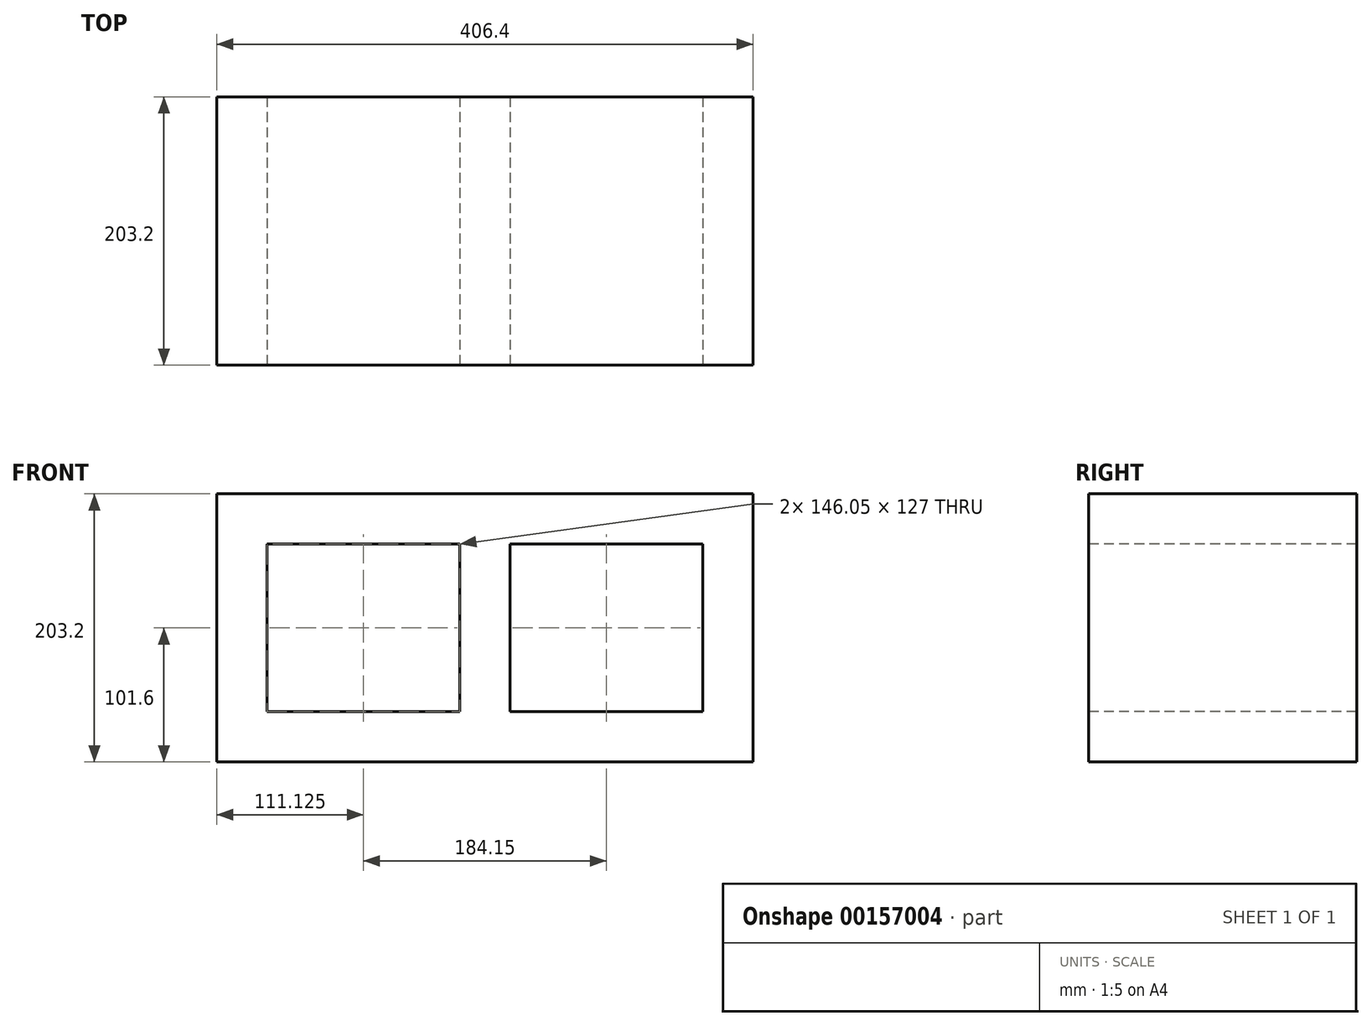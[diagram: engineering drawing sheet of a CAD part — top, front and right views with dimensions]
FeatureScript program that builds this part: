
annotation { "Feature Type Name" : "Feature", "Feature Type Description" : "" }
export const myFeature = defineFeature(function(context is Context, id is Id, definition is map)
    precondition{}
    {
        {
            var Q0;
            Q0=qCreatedBy(makeId("Front.planeOp"),FACE);
            var sketch = newSketch(context, id + "F0", { "sketchPlane" : qUnion([Q0])});
            skLineSegment(sketch, "E0.bottom", {"start": v(-203.2, 101.6) * mm, "end": v(203.2, 101.6) * mm});
            skLineSegment(sketch, "E0.top", {"start": v(-203.2, -101.6) * mm, "end": v(203.2, -101.6) * mm});
            skLineSegment(sketch, "E0.left", {"start": v(-203.2, 101.6) * mm, "end": v(-203.2, -101.6) * mm});
            skLineSegment(sketch, "E0.right", {"start": v(203.2, 101.6) * mm, "end": v(203.2, -101.6) * mm});
            skPoint(sketch, "E0.middle", {"position": v(0, 0) * mm});
            skLineSegment(sketch, "E1.bottom", {"start": v(-165.1, 63.5) * mm, "end": v(-19.05, 63.5) * mm});
            skLineSegment(sketch, "E1.top", {"start": v(-165.1, -63.5) * mm, "end": v(-19.05, -63.5) * mm});
            skLineSegment(sketch, "E1.left", {"start": v(-165.1, 63.5) * mm, "end": v(-165.1, -63.5) * mm});
            skLineSegment(sketch, "E1.right", {"start": v(-19.05, 63.5) * mm, "end": v(-19.05, -63.5) * mm});
            skPoint(sketch, "E1.middle", {"position": v(-92.07, 0) * mm});
            skLineSegment(sketch, "E2.bottom", {"start": v(19.05, 63.5) * mm, "end": v(165.1, 63.5) * mm});
            skLineSegment(sketch, "E2.top", {"start": v(19.05, -63.5) * mm, "end": v(165.1, -63.5) * mm});
            skLineSegment(sketch, "E2.left", {"start": v(19.05, 63.5) * mm, "end": v(19.05, -63.5) * mm});
            skLineSegment(sketch, "E2.right", {"start": v(165.1, 63.5) * mm, "end": v(165.1, -63.5) * mm});
            skPoint(sketch, "E2.middle", {"position": v(92.08, 0) * mm});
            skSolve(sketch);
        }
        {
            var Q0;
            Q0=makeQuery(id+"F0.imprint","IMPRINT",FACE,{"disambiguationData":[TD([[makeQuery(id+"F0.imprint","IMPRINT",EDGE,{"derivedFrom":sQuery(id+"F0.wireOp",EDGE,"E0.bottom")}),-1.0]])]});
            extrude(context, id + "F1", {"entities" : qUnion([Q0]), "oppositeDirection" : true, "depth" : 203.2 * mm});
        }
    });
